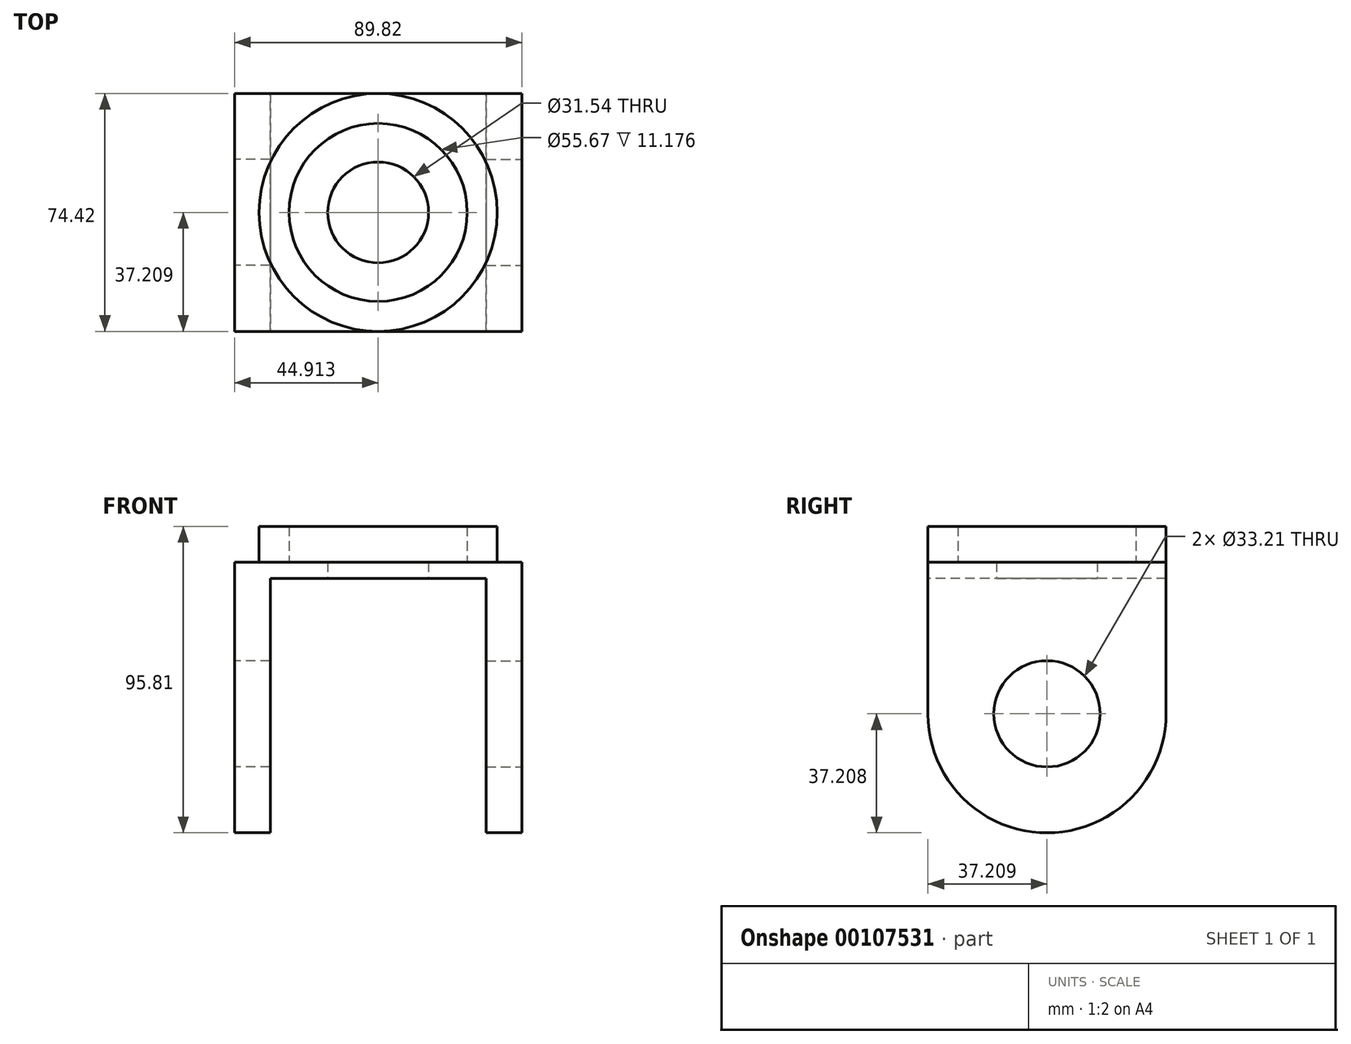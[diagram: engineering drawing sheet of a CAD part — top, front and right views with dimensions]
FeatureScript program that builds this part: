
annotation { "Feature Type Name" : "Feature", "Feature Type Description" : "" }
export const myFeature = defineFeature(function(context is Context, id is Id, definition is map)
    precondition{}
    {
        {
            var Q0;
            Q0=qCreatedBy(makeId("Top.planeOp"),FACE);
            var sketch = newSketch(context, id + "F0", { "sketchPlane" : qUnion([Q0])});
            skLineSegment(sketch, "E0.bottom", {"start": v(-103.64, 31.07) * mm, "end": v(-13.82, 31.07) * mm});
            skLineSegment(sketch, "E0.top", {"start": v(-103.64, -43.35) * mm, "end": v(-13.82, -43.35) * mm});
            skLineSegment(sketch, "E0.left", {"start": v(-103.64, 31.07) * mm, "end": v(-103.64, -43.35) * mm});
            skLineSegment(sketch, "E0.right", {"start": v(-13.82, 31.07) * mm, "end": v(-13.82, -43.35) * mm});
            skCircle(sketch, "E1", {"center": v(-58.73, -6.14) * mm, "radius": 15.77 * mm});
            skLineSegment(sketch, "E2", {"start": v(-58.73, 31.07) * mm, "end": v(-58.73, -43.35) * mm});
            skSolve(sketch);
        }
        {
            var Q0;
            {var subQ4=sQuery(id+"F0.wireOp",EDGE,"E0.right");Q0=makeQuery(id+"F0.imprint","IMPRINT",FACE,{"disambiguationData":[TD([[makeQuery(id+"F0.imprint","IMPRINT",EDGE,{"derivedFrom":subQ4}),-1.0]])]});}
            extrude(context, id + "F1", {"entities" : qUnion([Q0]), "depth" : 5.08 * mm});
        }
        {
            var Q0;
            Q0=makeQuery(id+"F1.opExtrude","CAP_FACE",FACE,{"disambiguationData":[OSD([sQuery(id+"F0.wireOp",EDGE,"E0.bottom"),sQuery(id+"F0.wireOp",EDGE,"E0.top"),sQuery(id+"F0.wireOp",EDGE,"E0.right"),sQuery(id+"F0.wireOp",EDGE,"E1"),sQuery(id+"F0.wireOp",EDGE,"E2")])],"isStart":false});
            var sketch = newSketch(context, id + "F2", { "sketchPlane" : qUnion([Q0])});
            skCircle(sketch, "E3", {"center": v(-58.73, -6.14) * mm, "radius": 37.2 * mm});
            skCircle(sketch, "E4", {"center": v(-58.73, -6.14) * mm, "radius": 27.84 * mm});
            skSolve(sketch);
        }
        {
            var Q0;
            {var subQ1=sQuery(id+"F0.wireOp",EDGE,"E2");var subQ2=sQuery(id+"F0.wireOp",EDGE,"E0.bottom");var subQ4=makeQuery(id+"F1.opExtrude","CAP_EDGE",EDGE,{"disambiguationData":[OSD([subQ1]),TDD([makeQuery(id+"F0.imprint","IMPRINT",EDGE,{"disambiguationData":[TD([[makeQuery(id+"F0.imprint","INTERSECT",VERTEX,{"derivedFrom":[subQ2,subQ1]}),-1.0]])],"derivedFrom":subQ1})])],"isStart":false});var subQ9=sQuery(id+"F2.wireOp",EDGE,"E4");var subQ10=makeQuery(id+"F2.imprint","INTERSECT",VERTEX,{"derivedFrom":[subQ4,subQ9]});Q0=makeQuery(id+"F2.imprint","IMPRINT",FACE,{"disambiguationData":[TD([[makeQuery(id+"F2.imprint","IMPRINT",EDGE,{"disambiguationData":[TD([[subQ10,1.0]])],"derivedFrom":subQ9}),-1.0]])]});}
            extrude(context, id + "F3", {"entities" : qUnion([Q0]), "operationType" : NewBodyOperationType.ADD, "depth" : 11.18 * mm});
        }
        {
            var Q0;
            Q0=makeQuery(id+"F1.opExtrude","SWEPT_FACE",FACE,{"disambiguationData":[OSD([sQuery(id+"F0.wireOp",EDGE,"E0.right")])]});
            var sketch = newSketch(context, id + "F4", { "sketchPlane" : qUnion([Q0])});
            skLineSegment(sketch, "E5", {"start": v(-43.35, 0) * mm, "end": v(-43.35, -42.43) * mm});
            skLineSegment(sketch, "E6", {"start": v(31.07, 0) * mm, "end": v(31.07, -42.25) * mm});
            skLineSegment(sketch, "E7", {"start": v(31.07, -42.25) * mm, "end": v(-43.35, -42.43) * mm});
            skCircle(sketch, "E8", {"center": v(-6.14, -42.34) * mm, "radius": 37.2 * mm});
            skCircle(sketch, "E9", {"center": v(-6.14, -42.34) * mm, "radius": 16.6 * mm});
            skSolve(sketch);
        }
        {
            var Q0;
            {var subQ5=sQuery(id+"F4.wireOp",EDGE,"E6");Q0=makeQuery(id+"F4.imprint","IMPRINT",FACE,{"disambiguationData":[TD([[makeQuery(id+"F4.imprint","IMPRINT",EDGE,{"derivedFrom":subQ5}),-1.0]])]});}
            var Q1;
            {var subQ1=sQuery(id+"F4.wireOp",EDGE,"E7");var subQ5=sQuery(id+"F4.wireOp",EDGE,"E9");var subQ6=makeQuery(id+"F4.imprint","INTERSECT",VERTEX,{"disambiguationData":[OD(0.0)],"derivedFrom":[subQ1,subQ5]});Q1=makeQuery(id+"F4.imprint","IMPRINT",FACE,{"disambiguationData":[TD([[makeQuery(id+"F4.imprint","IMPRINT",EDGE,{"disambiguationData":[TD([[subQ6,-1.0]])],"derivedFrom":subQ5}),-1.0]])]});}
            var Q2;
            {var subQ1=sQuery(id+"F4.wireOp",EDGE,"E7");var subQ3=sQuery(id+"F4.wireOp",EDGE,"E9");var subQ4=makeQuery(id+"F4.imprint","INTERSECT",VERTEX,{"disambiguationData":[OD(0.0)],"derivedFrom":[subQ1,subQ3]});Q2=makeQuery(id+"F4.imprint","IMPRINT",FACE,{"disambiguationData":[TD([[makeQuery(id+"F4.imprint","IMPRINT",EDGE,{"disambiguationData":[TD([[subQ4,1.0]])],"derivedFrom":subQ3}),-1.0]])]});}
            extrude(context, id + "F5", {"entities" : qUnion([Q0, Q1, Q2]), "operationType" : NewBodyOperationType.ADD, "oppositeDirection" : true, "depth" : 11.18 * mm});
        }
        {
            var Q0;
            Q0=makeQuery(id+"F1.opExtrude","SWEPT_BODY",BODY,{"disambiguationData":[OSD([sQuery(id+"F0.wireOp",EDGE,"E0.bottom"),sQuery(id+"F0.wireOp",EDGE,"E0.top"),sQuery(id+"F0.wireOp",EDGE,"E0.right"),sQuery(id+"F0.wireOp",EDGE,"E1"),sQuery(id+"F0.wireOp",EDGE,"E2")])]});
            var Q1;
            {var subQ0=sQuery(id+"F0.wireOp",EDGE,"E2");var subQ1=sQuery(id+"F0.wireOp",EDGE,"E0.top");var subQ2=makeQuery(id+"F0.imprint","IMPRINT",EDGE,{"disambiguationData":[TD([[makeQuery(id+"F0.imprint","INTERSECT",VERTEX,{"derivedFrom":[subQ1,subQ0]}),1.0]])],"derivedFrom":subQ0});var subQ3=makeQuery(id+"F1.opExtrude","CAP_EDGE",EDGE,{"disambiguationData":[OSD([subQ0]),TDD([subQ2])],"isStart":false});Q1=makeQuery(id+"F3.boolean.opBoolean","MERGE",FACE,{"derivedFrom":[makeQuery(id+"F1.opExtrude","SWEPT_FACE",FACE,{"disambiguationData":[OSD([subQ0]),TDD([subQ2])]}),makeQuery(id+"F3.opExtrude","SWEPT_FACE",FACE,{"disambiguationData":[OSD([subQ0]),TDD([makeQuery(id+"F2.imprint","IMPRINT",EDGE,{"disambiguationData":[TD([[makeQuery(id+"F2.imprint","INTERSECT",VERTEX,{"derivedFrom":[subQ3,sQuery(id+"F2.wireOp",EDGE,"E4")]}),-1.0]])],"derivedFrom":subQ3})])]})]});}
            mirror(context, id + "F6", {"operationType" : NewBodyOperationType.ADD, "entities" : qUnion([Q0]), "mirrorPlane" : qUnion([Q1])});
        }
    });
